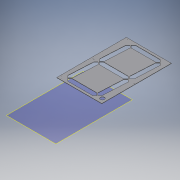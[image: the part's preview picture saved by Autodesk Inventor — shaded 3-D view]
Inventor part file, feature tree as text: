
AUTODESK INVENTOR PART (.ipt)
format: ipt  version: 2016 SP2 (Build 200236200, 236)  size: 175,616 bytes
history: native  units: mm
features: reference x49, extrude x2, sketch x2, plane x1
ambient origin geometry x8: Origin, YZ Plane, XZ Plane, XY Plane, X Axis, Y Axis, Z Axis, Center Point
bodies: Body1 (feature_tree)
feature tree (54):
  extrude  "Extrusion2"  Depth=4.5mm
  extrude  "Extrusion3"  Depth=0.6mm TaperAngle=0.0deg
  plane  "Arbeitsebene1"
  sketch  "Skizze1"  dims[d2=9.0mm d3=4.5mm]
  reference  "Referenz1"
  reference  "Referenz4"
  reference  "Referenz7"
  reference  "Referenz8"
  reference  "Referenz9"
  reference  "Referenz10"
  reference  "Referenz11"
  reference  "Referenz12"
  reference  "Referenz13"
  reference  "Referenz14"
  reference  "Referenz15"
  reference  "Referenz16"
  reference  "Referenz17"
  reference  "Referenz18"
  reference  "Referenz19"
  reference  "Referenz20"
  reference  "Referenz21"
  reference  "Referenz22"
  reference  "Referenz23"
  reference  "Referenz24"
  reference  "Referenz25"
  reference  "Referenz26"
  reference  "Referenz27"
  reference  "Referenz28"
  reference  "Referenz29"
  reference  "Referenz30"
  reference  "Referenz31"
  reference  "Referenz32"
  reference  "Referenz33"
  reference  "Referenz34"
  reference  "Referenz35"
  reference  "Referenz36"
  reference  "Referenz37"
  reference  "Referenz38"
  reference  "Referenz39"
  reference  "Referenz40"
  reference  "Referenz41"
  reference  "Referenz42"
  reference  "Referenz43"
  reference  "Referenz44"
  reference  "Referenz45"
  reference  "Referenz46"
  reference  "Referenz47"
  sketch  "Skizze2"  dims[d4=4.5mm d5=0.6mm d6=0.0mm d7=4.8mm d8=4.8mm d9=4.8mm d10=4.8mm d11=4.8mm d12=2.6mm d13=0.0mm d14=4.8mm]
  reference  "Referenz48"
  reference  "Referenz49"
  reference  "Referenz50"
  reference  "Referenz51"
  reference  "Referenz52"
  reference  "Referenz56"
